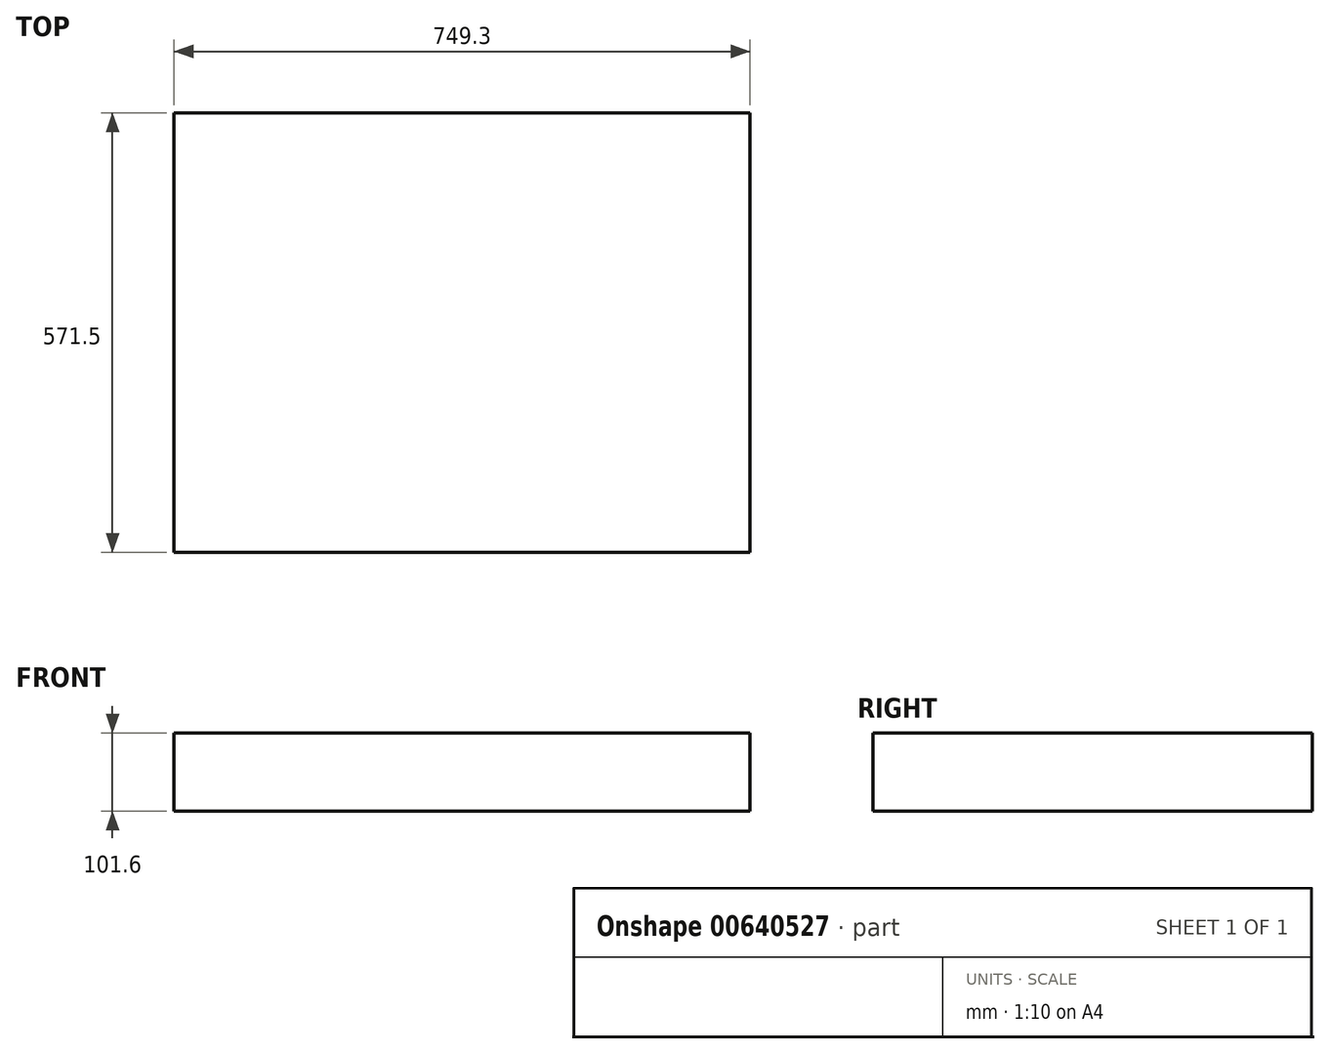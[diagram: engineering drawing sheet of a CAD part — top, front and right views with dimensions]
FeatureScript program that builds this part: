
annotation { "Feature Type Name" : "Feature", "Feature Type Description" : "" }
export const myFeature = defineFeature(function(context is Context, id is Id, definition is map)
    precondition{}
    {
        {
            var Q0;
            Q0=qCreatedBy(makeId("Top.planeOp"),FACE);
            var sketch = newSketch(context, id + "F0", { "sketchPlane" : qUnion([Q0])});
            skLineSegment(sketch, "E0.bottom", {"start": v(-374.65, 285.75) * mm, "end": v(374.65, 285.75) * mm});
            skLineSegment(sketch, "E0.top", {"start": v(-374.65, -285.75) * mm, "end": v(374.65, -285.75) * mm});
            skLineSegment(sketch, "E0.left", {"start": v(-374.65, 285.75) * mm, "end": v(-374.65, -285.75) * mm});
            skLineSegment(sketch, "E0.right", {"start": v(374.65, 285.75) * mm, "end": v(374.65, -285.75) * mm});
            skPoint(sketch, "E0.middle", {"position": v(0, 0) * mm});
            skSolve(sketch);
        }
        {
            var Q0;
            Q0=makeQuery(id+"F0.imprint","IMPRINT",FACE,{"disambiguationData":[TD([[makeQuery(id+"F0.imprint","IMPRINT",EDGE,{"derivedFrom":sQuery(id+"F0.wireOp",EDGE,"E0.bottom")}),-1.0]])]});
            extrude(context, id + "F1", {"entities" : qUnion([Q0]), "depth" : 101.6 * mm, "offsetDistance" : 25.4 * mm});
        }
    });
